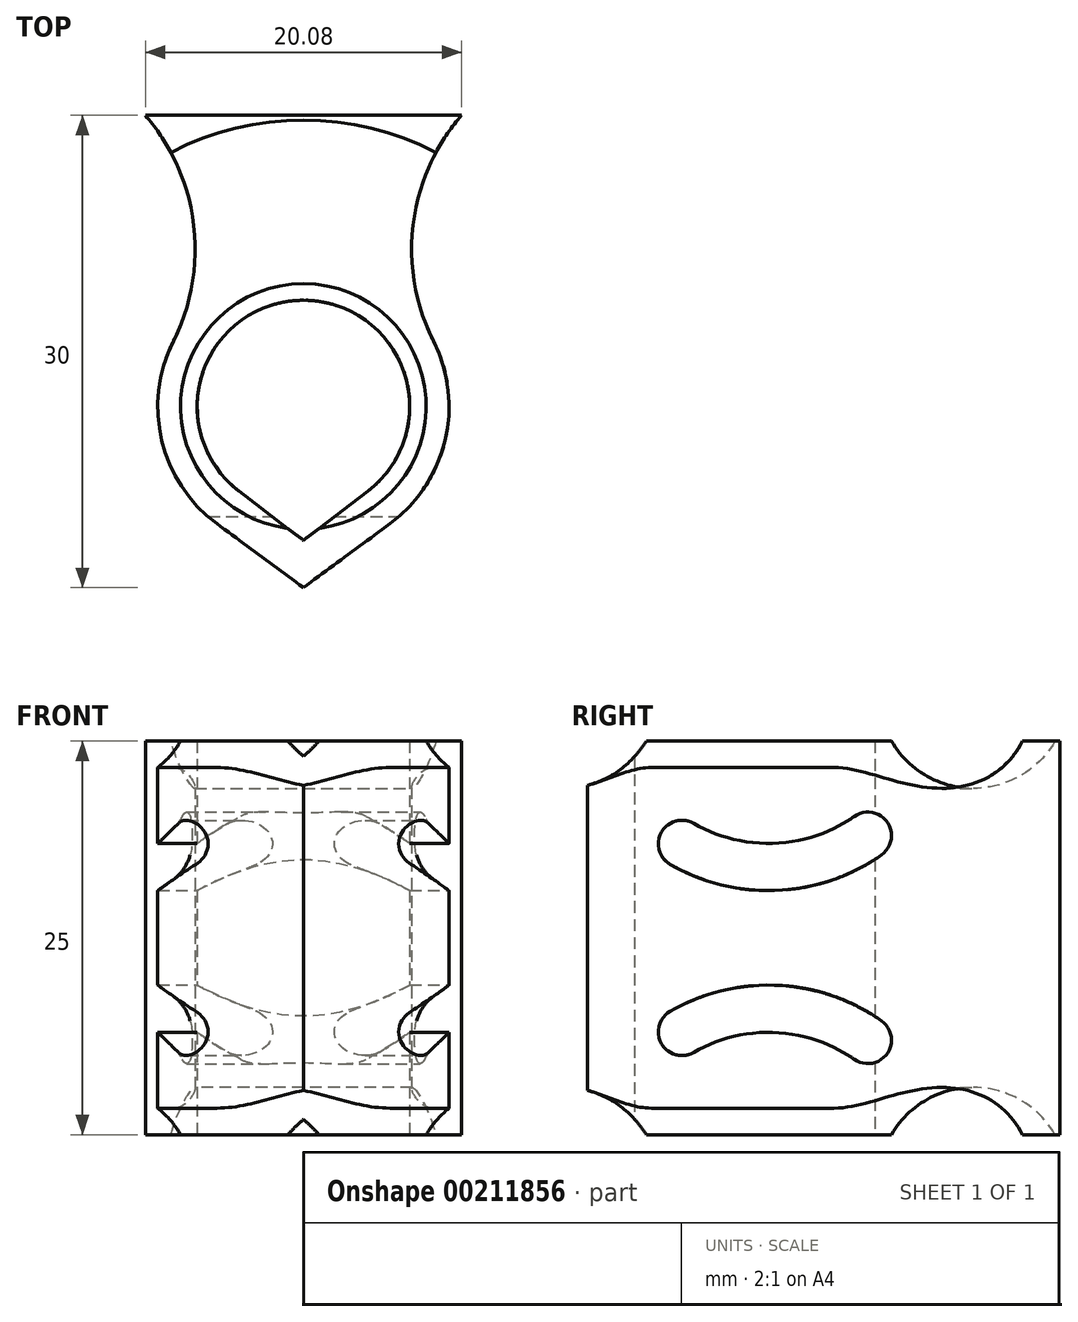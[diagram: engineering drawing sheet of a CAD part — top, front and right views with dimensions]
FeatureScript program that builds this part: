
annotation { "Feature Type Name" : "Feature", "Feature Type Description" : "" }
export const myFeature = defineFeature(function(context is Context, id is Id, definition is map)
    precondition{}
    {
        {
            var Q0;
            Q0=qCreatedBy(makeId("Top.planeOp"),FACE);
            var sketch = newSketch(context, id + "F0", { "sketchPlane" : qUnion([Q0])});
            skArc(sketch, "E0", {"start": v(4.1, -5.36) * mm, "mid": v(0, 6.75) * mm, "end": v(-4.1, -5.36) * mm});
            skArc(sketch, "E1", {"start": v(5.5, -7.44) * mm, "mid": v(0, 9.25) * mm, "end": v(-5.5, -7.44) * mm});
            skLineSegment(sketch, "E2", {"start": v(10.04, 18.5) * mm, "end": v(-10.04, 18.5) * mm});
            skArc(sketch, "E3", {"start": v(-8.26, 4.16) * mm, "mid": v(-6.97, 11.6) * mm, "end": v(-10.04, 18.5) * mm});
            skArc(sketch, "E4", {"start": v(10.04, 18.5) * mm, "mid": v(6.97, 11.6) * mm, "end": v(8.26, 4.16) * mm});
            skLineSegment(sketch, "E5", {"start": v(-27.32, 10) * mm, "end": v(39.04, 10) * mm, "construction": true});
            skLineSegment(sketch, "E6", {"start": v(-4.1, -5.36) * mm, "end": v(0, -8.5) * mm});
            skLineSegment(sketch, "E7", {"start": v(0, -8.5) * mm, "end": v(4.1, -5.36) * mm});
            skLineSegment(sketch, "E8", {"start": v(-5.5, -7.44) * mm, "end": v(0, -11.5) * mm});
            skLineSegment(sketch, "E9", {"start": v(0, -11.5) * mm, "end": v(5.5, -7.44) * mm});
            skSolve(sketch);
        }
        {
            var Q0;
            Q0=makeQuery(id+"F0.imprint","IMPRINT",FACE,{"disambiguationData":[TD([[makeQuery(id+"F0.imprint","IMPRINT",EDGE,{"derivedFrom":sQuery(id+"F0.wireOp",EDGE,"E2")}),1.0]])]});
            var Q1;
            Q1=makeQuery(id+"F0.imprint","IMPRINT",FACE,{"disambiguationData":[TD([[makeQuery(id+"F0.imprint","IMPRINT",EDGE,{"derivedFrom":sQuery(id+"F0.wireOp",EDGE,"E0")}),-1.0]])]});
            extrude(context, id + "F1", {"entities" : qUnion([Q0, Q1]), "depth" : 25 * mm, "offsetDistance" : 25 * mm});
        }
        {
            var Q0;
            Q0=qCreatedBy(makeId("Front.planeOp"),FACE);
            var sketch = newSketch(context, id + "F2", { "sketchPlane" : qUnion([Q0])});
            skCircle(sketch, "E10", {"center": v(13, 28) * mm, "radius": 6 * mm});
            skCircle(sketch, "E11", {"center": v(13, -3) * mm, "radius": 6 * mm});
            skLineSegment(sketch, "E12", {"start": v(13, 28) * mm, "end": v(13, 25) * mm, "construction": true});
            skLineSegment(sketch, "E13", {"start": v(13, 25) * mm, "end": v(10.04, 25) * mm, "construction": true});
            skLineSegment(sketch, "E14", {"start": v(10.04, 0) * mm, "end": v(13, 0) * mm, "construction": true});
            skLineSegment(sketch, "E15", {"start": v(13, 0) * mm, "end": v(13, -3) * mm, "construction": true});
            skSolve(sketch);
        }
        {
            var Q0;
            Q0 = qSketchRegion(id + "F2", true);
            var Q1;
            Q1=makeQuery(id+"F1.opExtrude","SWEPT_FACE",FACE,{"disambiguationData":[OSD([sQuery(id+"F0.wireOp",EDGE,"E0")])]});
            revolve(context, id + "F3", {"operationType" : NewBodyOperationType.REMOVE, "entities" : qUnion([Q0]), "axis" : qUnion([Q1]), "revolveType" : RevolveType.FULL, "oppositeDirection" : true});
        }
        {
            var Q0;
            Q0=qCreatedBy(makeId("Right.planeOp"),FACE);
            var sketch = newSketch(context, id + "F4", { "sketchPlane" : qUnion([Q0])});
            skArc(sketch, "E16", {"start": v(-4.75, 19.77) * mm, "mid": v(0.41, 18.5) * mm, "end": v(5.45, 20.22) * mm});
            skArc(sketch, "E17", {"start": v(-6.25, 17.17) * mm, "mid": v(0.55, 15.51) * mm, "end": v(7.17, 17.76) * mm});
            skArc(sketch, "E18", {"start": v(5.45, 4.78) * mm, "mid": v(0.41, 6.5) * mm, "end": v(-4.75, 5.23) * mm});
            skArc(sketch, "E19", {"start": v(7.17, 7.24) * mm, "mid": v(0.55, 9.49) * mm, "end": v(-6.25, 7.83) * mm});
            skArc(sketch, "E20", {"start": v(5.45, 4.78) * mm, "mid": v(7.54, 5.15) * mm, "end": v(7.17, 7.24) * mm});
            skArc(sketch, "E21", {"start": v(-6.25, 7.83) * mm, "mid": v(-6.8, 5.78) * mm, "end": v(-4.75, 5.23) * mm});
            skArc(sketch, "E22", {"start": v(-4.75, 19.77) * mm, "mid": v(-6.8, 19.22) * mm, "end": v(-6.25, 17.17) * mm});
            skArc(sketch, "E23", {"start": v(7.17, 17.76) * mm, "mid": v(7.54, 19.85) * mm, "end": v(5.45, 20.22) * mm});
            skLineSegment(sketch, "E24", {"start": v(0, 28) * mm, "end": v(-5.5, 18.47) * mm, "construction": true});
            skLineSegment(sketch, "E25", {"start": v(0, 28) * mm, "end": v(6.3, 18.99) * mm, "construction": true});
            skLineSegment(sketch, "E26", {"start": v(0, 40.05) * mm, "end": v(0, -32.13) * mm, "construction": true});
            skLineSegment(sketch, "E27", {"start": v(-5.5, 6.53) * mm, "end": v(0, -3) * mm, "construction": true});
            skLineSegment(sketch, "E28", {"start": v(0, -3) * mm, "end": v(6.3, 6.01) * mm, "construction": true});
            skSolve(sketch);
        }
        {
            var Q0;
            Q0 = qSketchRegion(id + "F4", true);
            extrude(context, id + "F5", {"entities" : qUnion([Q0]), "operationType" : NewBodyOperationType.REMOVE, "oppositeDirection" : true, "depth" : 25 * mm, "offsetDistance" : 25 * mm, "symmetric" : true});
        }
    });
